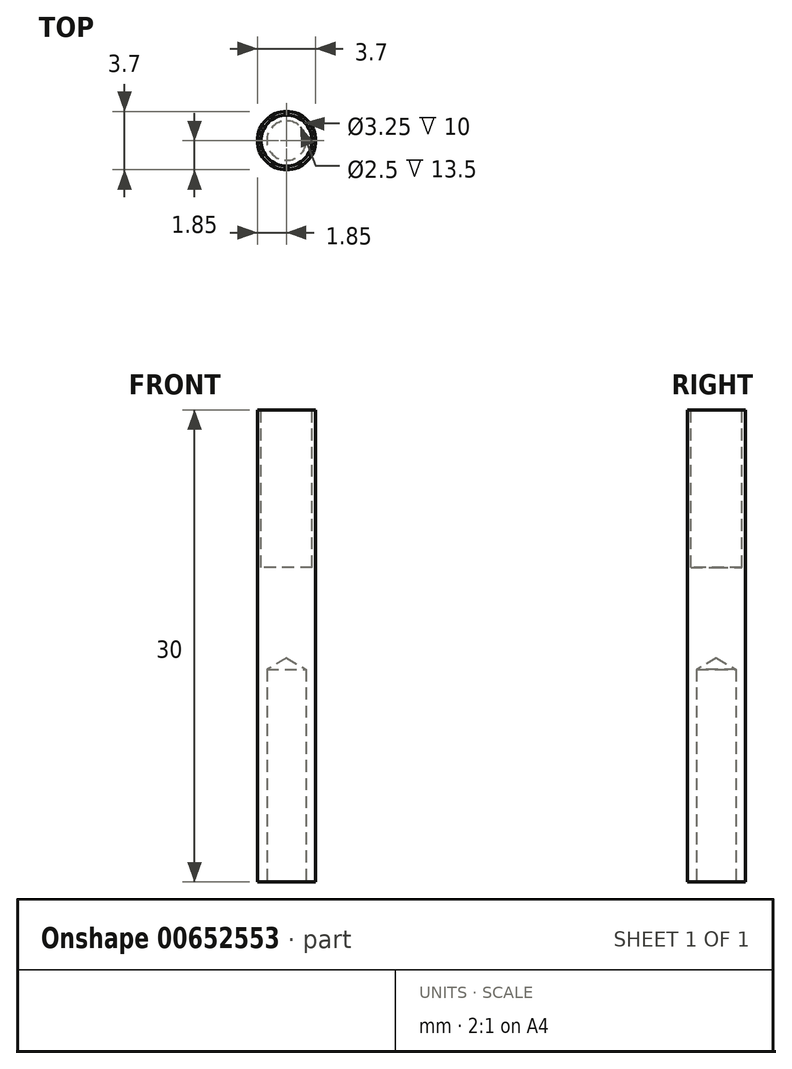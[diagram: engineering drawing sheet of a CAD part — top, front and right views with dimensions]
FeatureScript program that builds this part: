
annotation { "Feature Type Name" : "Feature", "Feature Type Description" : "" }
export const myFeature = defineFeature(function(context is Context, id is Id, definition is map)
    precondition{}
    {
        {
            var Q0;
            Q0=qCreatedBy(makeId("Top.planeOp"),FACE);
            var sketch = newSketch(context, id + "F0", { "sketchPlane" : qUnion([Q0])});
            skCircle(sketch, "E0", {"center": v(0, 0) * mm, "radius": 1.85 * mm});
            skSolve(sketch);
        }
        {
            var Q0;
            Q0 = qSketchRegion(id + "F0", true);
            extrude(context, id + "F1", {"entities" : qUnion([Q0]), "depth" : 30 * mm, "offsetDistance" : 25 * mm});
        }
        {
            var Q0;
            Q0=makeQuery(id+"F1.opExtrude","CAP_FACE",FACE,{"disambiguationData":[OSD([sQuery(id+"F0.wireOp",EDGE,"E0")])],"isStart":false});
            var sketch = newSketch(context, id + "F2", { "sketchPlane" : qUnion([Q0])});
            skCircle(sketch, "E1", {"center": v(0, 0) * mm, "radius": 1.63 * mm});
            skSolve(sketch);
        }
        {
            var Q0;
            Q0 = qSketchRegion(id + "F2", true);
            extrude(context, id + "F3", {"entities" : qUnion([Q0]), "operationType" : NewBodyOperationType.REMOVE, "oppositeDirection" : true, "depth" : 10 * mm, "offsetDistance" : 25 * mm});
        }
        {
            var Q0;
            Q0=makeQuery(id+"F1.opExtrude","CAP_FACE",FACE,{"disambiguationData":[OSD([sQuery(id+"F0.wireOp",EDGE,"E0")])],"isStart":true});
            var sketch = newSketch(context, id + "F4", { "sketchPlane" : qUnion([Q0])});
            skPoint(sketch, "E2", {"position": v(0, 0) * mm});
            skSolve(sketch);
        }
        {
            var Q0;
            Q0=sQuery(id+"F4.wireOp",VERTEX,"E2");
            var Q1;
            Q1=makeQuery(id+"F1.opExtrude","SWEPT_BODY",BODY,{"disambiguationData":[OSD([sQuery(id+"F0.wireOp",EDGE,"E0")])]});
            hole(context, id + "F5", {"style" : HoleStyle.SIMPLE, "endStyle" : HoleEndStyle.BLIND, "standardTappedOrClearance" : lookupTablePath({ "standard" : "ISO", "engagement" : "75%", "pitch" : "0.5 mm", "size" : "M3", "type" : "Tapped" }), "standardBlindInLast" : lookupTablePath({ "standard" : "ISO", "engagement" : "75%", "pitch" : "0.5 mm", "size" : "M3", "type" : "Tapped" }), "holeDiameter" : 2.5 * mm, "majorDiameter" : 3 * mm, "showTappedDepth" : true, "holeDepth" : 13.5 * mm, "isTappedThrough" : true, "tappedDepth" : 12 * mm, "tapClearance" : 3, "locations" : qUnion([Q0]), "scope" : qUnion([Q1])});
        }
    });
